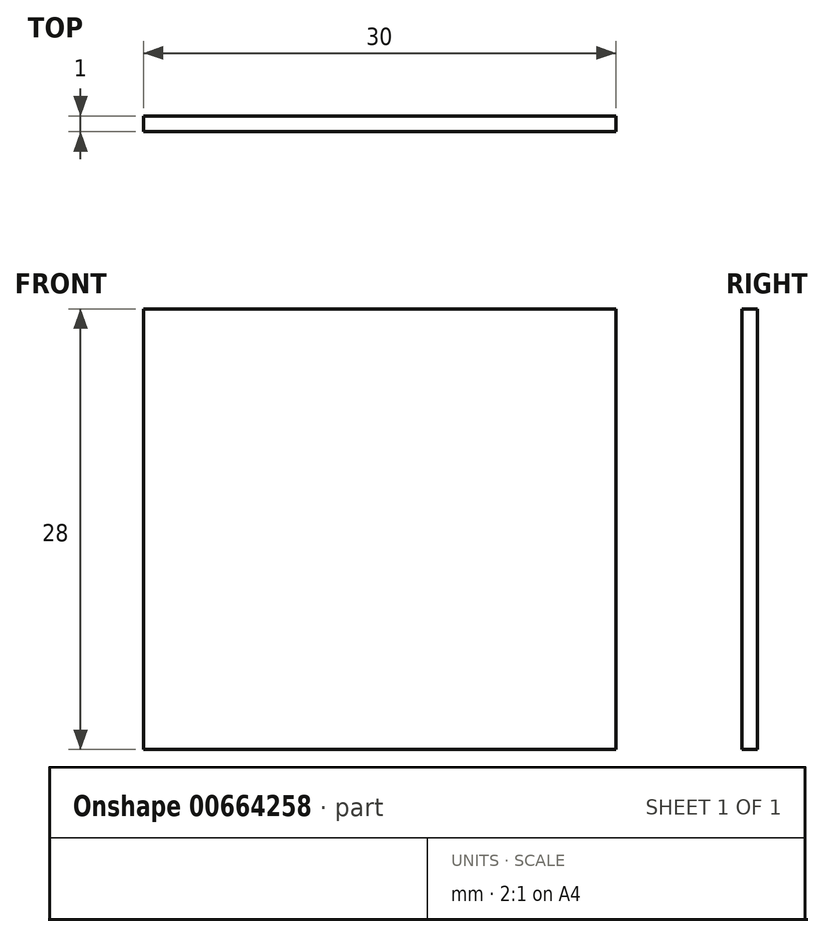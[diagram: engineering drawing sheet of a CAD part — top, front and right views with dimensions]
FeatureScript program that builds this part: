
annotation { "Feature Type Name" : "Feature", "Feature Type Description" : "" }
export const myFeature = defineFeature(function(context is Context, id is Id, definition is map)
    precondition{}
    {
        {
            var Q0;
            Q0=qCreatedBy(makeId("Front.planeOp"),FACE);
            var sketch = newSketch(context, id + "F0", { "sketchPlane" : qUnion([Q0])});
            skLineSegment(sketch, "E0.bottom", {"start": v(15, 14) * mm, "end": v(-15, 14) * mm});
            skLineSegment(sketch, "E0.top", {"start": v(15, -14) * mm, "end": v(-15, -14) * mm});
            skLineSegment(sketch, "E0.left", {"start": v(15, 14) * mm, "end": v(15, -14) * mm});
            skLineSegment(sketch, "E0.right", {"start": v(-15, 14) * mm, "end": v(-15, -14) * mm});
            skPoint(sketch, "E0.middle", {"position": v(0, 0) * mm});
            skSolve(sketch);
        }
        {
            var Q0;
            Q0=makeQuery(id+"F0.imprint","IMPRINT",FACE,{"disambiguationData":[TD([[makeQuery(id+"F0.imprint","IMPRINT",EDGE,{"derivedFrom":sQuery(id+"F0.wireOp",EDGE,"E0.bottom")}),1.0]])]});
            extrude(context, id + "F1", {"entities" : qUnion([Q0]), "depth" : 1 * mm, "offsetDistance" : 25 * mm});
        }
    });
